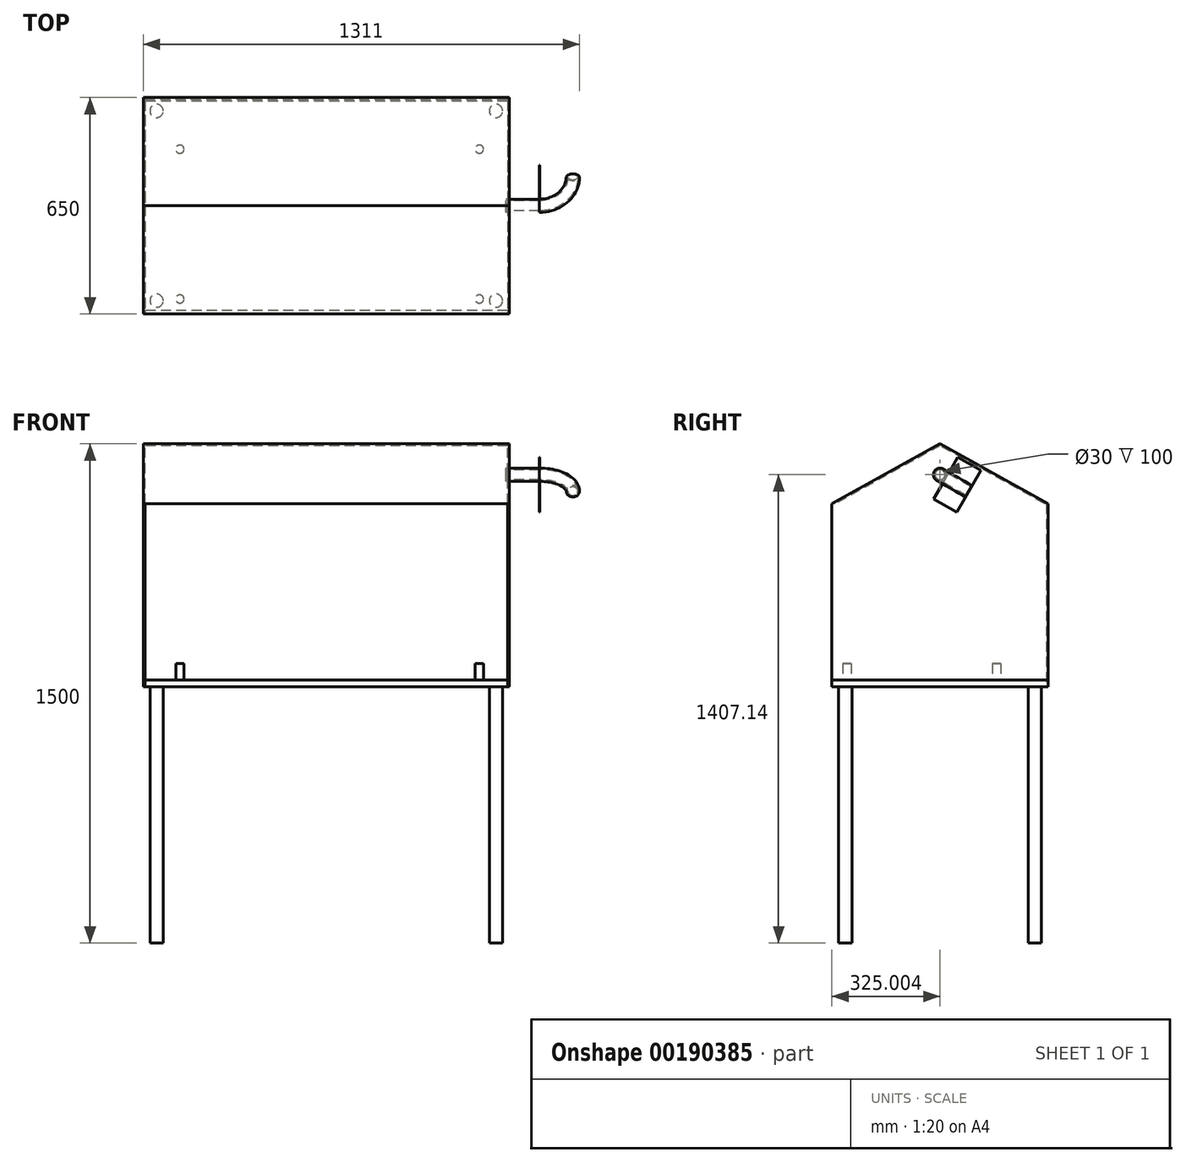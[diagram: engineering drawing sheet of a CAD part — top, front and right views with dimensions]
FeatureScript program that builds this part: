
annotation { "Feature Type Name" : "Feature", "Feature Type Description" : "" }
export const myFeature = defineFeature(function(context is Context, id is Id, definition is map)
    precondition{}
    {
        {
            var Q0;
            Q0=qCreatedBy(makeId("Top.planeOp"),FACE);
            var sketch = newSketch(context, id + "F0", { "sketchPlane" : qUnion([Q0])});
            skLineSegment(sketch, "E0.bottom", {"start": v(-6.1, 666.7) * mm, "end": v(1093.9, 666.7) * mm});
            skLineSegment(sketch, "E0.top", {"start": v(-6.1, 16.7) * mm, "end": v(1093.9, 16.7) * mm});
            skLineSegment(sketch, "E0.left", {"start": v(-6.1, 666.7) * mm, "end": v(-6.1, 16.7) * mm});
            skLineSegment(sketch, "E0.right", {"start": v(1093.9, 666.7) * mm, "end": v(1093.9, 16.7) * mm});
            skLineSegment(sketch, "E1.0", {"start": v(33.9, 626.7) * mm, "end": v(1053.9, 626.7) * mm, "construction": true});
            skLineSegment(sketch, "E1.1", {"start": v(33.9, 626.7) * mm, "end": v(33.9, 56.7) * mm, "construction": true});
            skLineSegment(sketch, "E1.2", {"start": v(33.9, 56.7) * mm, "end": v(1053.9, 56.7) * mm, "construction": true});
            skLineSegment(sketch, "E1.3", {"start": v(1053.9, 626.7) * mm, "end": v(1053.9, 56.7) * mm, "construction": true});
            skCircle(sketch, "E2", {"center": v(33.9, 626.7) * mm, "radius": 20 * mm});
            skCircle(sketch, "E3", {"center": v(1053.9, 626.7) * mm, "radius": 20 * mm});
            skCircle(sketch, "E4", {"center": v(33.9, 56.7) * mm, "radius": 20 * mm});
            skCircle(sketch, "E5", {"center": v(1053.9, 56.7) * mm, "radius": 20 * mm});
            skLineSegment(sketch, "E6.0", {"start": v(38.9, 621.7) * mm, "end": v(1048.9, 621.7) * mm, "construction": true});
            skLineSegment(sketch, "E6.1", {"start": v(38.9, 621.7) * mm, "end": v(38.9, 61.7) * mm, "construction": true});
            skLineSegment(sketch, "E6.2", {"start": v(38.9, 61.7) * mm, "end": v(1048.9, 61.7) * mm, "construction": true});
            skLineSegment(sketch, "E6.3", {"start": v(1048.9, 621.7) * mm, "end": v(1048.9, 61.7) * mm, "construction": true});
            skLineSegment(sketch, "E7", {"start": v(1098.9, 16.7) * mm, "end": v(1103.9, 16.7) * mm});
            skLineSegment(sketch, "E8", {"start": v(-11.1, 16.7) * mm, "end": v(-16.1, 16.7) * mm});
            skSolve(sketch);
        }
        {
            var Q0;
            Q0=makeQuery(id+"F0.imprint","IMPRINT",FACE,{"disambiguationData":[TD([[makeQuery(id+"F0.imprint","IMPRINT",EDGE,{"derivedFrom":sQuery(id+"F0.wireOp",EDGE,"E0.bottom")}),-1.0]])]});
            var Q1;
            Q1=makeQuery(id+"F0.imprint","IMPRINT",FACE,{"disambiguationData":[TD([[makeQuery(id+"F0.imprint","IMPRINT",EDGE,{"derivedFrom":sQuery(id+"F0.wireOp",EDGE,"E3")}),1.0]])]});
            var Q2;
            Q2=makeQuery(id+"F0.imprint","IMPRINT",FACE,{"disambiguationData":[TD([[makeQuery(id+"F0.imprint","IMPRINT",EDGE,{"derivedFrom":sQuery(id+"F0.wireOp",EDGE,"E5")}),1.0]])]});
            var Q3;
            Q3=makeQuery(id+"F0.imprint","IMPRINT",FACE,{"disambiguationData":[TD([[makeQuery(id+"F0.imprint","IMPRINT",EDGE,{"derivedFrom":sQuery(id+"F0.wireOp",EDGE,"E4")}),1.0]])]});
            var Q4;
            Q4=makeQuery(id+"F0.imprint","IMPRINT",FACE,{"disambiguationData":[TD([[makeQuery(id+"F0.imprint","IMPRINT",EDGE,{"derivedFrom":sQuery(id+"F0.wireOp",EDGE,"E2")}),1.0]])]});
            extrude(context, id + "F1", {"entities" : qUnion([Q0, Q1, Q2, Q3, Q4]), "depth" : 20 * mm});
        }
        {
            var Q0;
            Q0=makeQuery(id+"F0.imprint","IMPRINT",FACE,{"disambiguationData":[TD([[makeQuery(id+"F0.imprint","IMPRINT",EDGE,{"derivedFrom":sQuery(id+"F0.wireOp",EDGE,"E5")}),1.0]])]});
            var Q1;
            Q1=makeQuery(id+"F0.imprint","IMPRINT",FACE,{"disambiguationData":[TD([[makeQuery(id+"F0.imprint","IMPRINT",EDGE,{"derivedFrom":sQuery(id+"F0.wireOp",EDGE,"E3")}),1.0]])]});
            var Q2;
            Q2=makeQuery(id+"F0.imprint","IMPRINT",FACE,{"disambiguationData":[TD([[makeQuery(id+"F0.imprint","IMPRINT",EDGE,{"derivedFrom":sQuery(id+"F0.wireOp",EDGE,"E2")}),1.0]])]});
            var Q3;
            Q3=makeQuery(id+"F0.imprint","IMPRINT",FACE,{"disambiguationData":[TD([[makeQuery(id+"F0.imprint","IMPRINT",EDGE,{"derivedFrom":sQuery(id+"F0.wireOp",EDGE,"E4")}),1.0]])]});
            extrude(context, id + "F2", {"entities" : qUnion([Q0, Q1, Q2, Q3]), "operationType" : NewBodyOperationType.ADD, "oppositeDirection" : true, "depth" : 770 * mm});
        }
        {
            var Q0;
            Q0=makeQuery(id+"F1.opExtrude","CAP_FACE",FACE,{"disambiguationData":[OSD([sQuery(id+"F0.wireOp",EDGE,"E0.bottom"),sQuery(id+"F0.wireOp",EDGE,"E0.top"),sQuery(id+"F0.wireOp",EDGE,"E0.left"),sQuery(id+"F0.wireOp",EDGE,"E0.right")])],"isStart":false});
            var sketch = newSketch(context, id + "F3", { "sketchPlane" : qUnion([Q0])});
            skLineSegment(sketch, "E9.bottom", {"start": v(-6.1, 16.7) * mm, "end": v(1093.9, 16.7) * mm, "construction": true});
            skLineSegment(sketch, "E9.top", {"start": v(-6.1, 666.7) * mm, "end": v(1093.9, 666.7) * mm, "construction": true});
            skLineSegment(sketch, "E9.left", {"start": v(-6.1, 16.7) * mm, "end": v(-6.1, 666.7) * mm, "construction": true});
            skLineSegment(sketch, "E9.right", {"start": v(1093.9, 16.7) * mm, "end": v(1093.9, 666.7) * mm, "construction": true});
            skLineSegment(sketch, "E10.0", {"start": v(33.9, 626.7) * mm, "end": v(1003.9, 626.7) * mm, "construction": true});
            skLineSegment(sketch, "E10.1", {"start": v(33.9, 56.7) * mm, "end": v(33.9, 626.7) * mm, "construction": true});
            skLineSegment(sketch, "E10.2", {"start": v(33.9, 56.7) * mm, "end": v(1003.9, 56.7) * mm, "construction": true});
            skLineSegment(sketch, "E10.3", {"start": v(1003.9, 56.7) * mm, "end": v(1003.9, 626.7) * mm, "construction": true});
            skLineSegment(sketch, "E11", {"start": v(33.9, 511.7) * mm, "end": v(1003.9, 511.7) * mm, "construction": true});
            skLineSegment(sketch, "E12", {"start": v(33.9, 61.7) * mm, "end": v(1003.9, 61.7) * mm, "construction": true});
            skLineSegment(sketch, "E13.bottom", {"start": v(1003.9, 511.7) * mm, "end": v(103.9, 511.7) * mm, "construction": true});
            skLineSegment(sketch, "E13.top", {"start": v(1003.9, 61.7) * mm, "end": v(103.9, 61.7) * mm, "construction": true});
            skLineSegment(sketch, "E13.left", {"start": v(1003.9, 511.7) * mm, "end": v(1003.9, 61.7) * mm, "construction": true});
            skLineSegment(sketch, "E13.right", {"start": v(103.9, 511.7) * mm, "end": v(103.9, 61.7) * mm, "construction": true});
            skCircle(sketch, "E14", {"center": v(103.9, 511.7) * mm, "radius": 12.5 * mm});
            skCircle(sketch, "E15", {"center": v(103.9, 61.7) * mm, "radius": 12.5 * mm});
            skCircle(sketch, "E16", {"center": v(1003.9, 511.7) * mm, "radius": 12.5 * mm});
            skCircle(sketch, "E17", {"center": v(1003.9, 61.7) * mm, "radius": 12.5 * mm});
            skSolve(sketch);
        }
        {
            var Q0;
            Q0=makeQuery(id+"F3.imprint","IMPRINT",FACE,{"disambiguationData":[TD([[makeQuery(id+"F3.imprint","IMPRINT",EDGE,{"derivedFrom":sQuery(id+"F3.wireOp",EDGE,"E16")}),1.0]])]});
            var Q1;
            Q1=makeQuery(id+"F3.imprint","IMPRINT",FACE,{"disambiguationData":[TD([[makeQuery(id+"F3.imprint","IMPRINT",EDGE,{"derivedFrom":sQuery(id+"F3.wireOp",EDGE,"E17")}),1.0]])]});
            var Q2;
            Q2=makeQuery(id+"F3.imprint","IMPRINT",FACE,{"disambiguationData":[TD([[makeQuery(id+"F3.imprint","IMPRINT",EDGE,{"derivedFrom":sQuery(id+"F3.wireOp",EDGE,"E15")}),1.0]])]});
            var Q3;
            Q3=makeQuery(id+"F3.imprint","IMPRINT",FACE,{"disambiguationData":[TD([[makeQuery(id+"F3.imprint","IMPRINT",EDGE,{"derivedFrom":sQuery(id+"F3.wireOp",EDGE,"E14")}),1.0]])]});
            extrude(context, id + "F4", {"entities" : qUnion([Q0, Q1, Q2, Q3]), "operationType" : NewBodyOperationType.ADD, "depth" : 50 * mm});
        }
        {
            var Q0;
            Q0=qCreatedBy(makeId("Top.planeOp"),FACE);
            var sketch = newSketch(context, id + "F5", { "sketchPlane" : qUnion([Q0])});
            skLineSegment(sketch, "E18.0", {"start": v(-1.1, 661.7) * mm, "end": v(-1.1, 16.7) * mm});
            skLineSegment(sketch, "E18.1", {"start": v(-1.1, 661.7) * mm, "end": v(1088.9, 661.7) * mm});
            skLineSegment(sketch, "E18.2", {"start": v(1088.9, 661.7) * mm, "end": v(1088.9, 16.7) * mm});
            skLineSegment(sketch, "E19.0", {"start": v(-6.1, 666.7) * mm, "end": v(-6.1, 16.7) * mm});
            skLineSegment(sketch, "E19.1", {"start": v(-6.1, 666.7) * mm, "end": v(1093.9, 666.7) * mm});
            skLineSegment(sketch, "E19.2", {"start": v(1093.9, 666.7) * mm, "end": v(1093.9, 16.7) * mm});
            skLineSegment(sketch, "E20", {"start": v(-6.1, 16.7) * mm, "end": v(-1.1, 16.7) * mm});
            skLineSegment(sketch, "E21", {"start": v(1088.9, 16.7) * mm, "end": v(1093.9, 16.7) * mm});
            skSolve(sketch);
        }
        {
            var Q0;
            Q0=makeQuery(id+"F5.imprint","IMPRINT",FACE,{"disambiguationData":[TD([[makeQuery(id+"F5.imprint","IMPRINT",EDGE,{"derivedFrom":sQuery(id+"F5.wireOp",EDGE,"E18.0")}),-1.0]])]});
            extrude(context, id + "F6", {"entities" : qUnion([Q0]), "depth" : 550 * mm});
        }
        {
            var Q0;
            Q0=makeQuery(id+"F6.opExtrude","SWEPT_FACE",FACE,{"disambiguationData":[OSD([sQuery(id+"F5.wireOp",EDGE,"E19.0")])]});
            var sketch = newSketch(context, id + "F7", { "sketchPlane" : qUnion([Q0])});
            skLineSegment(sketch, "E22", {"start": v(-666.7, 550) * mm, "end": v(-341.7, 730) * mm});
            skPoint(sketch, "E22.endSnap0", {"position": v(-341.7, 550) * mm});
            skLineSegment(sketch, "E23", {"start": v(-341.7, 730) * mm, "end": v(-16.7, 550) * mm});
            skLineSegment(sketch, "E24.0", {"start": v(-341.7, 724.28) * mm, "end": v(-27.02, 550) * mm});
            skLineSegment(sketch, "E24.1", {"start": v(-656.38, 550) * mm, "end": v(-341.7, 724.28) * mm});
            skLineSegment(sketch, "E25", {"start": v(-16.7, 550) * mm, "end": v(-666.7, 550) * mm});
            skCircle(sketch, "E26", {"center": v(-341.7, 637.14) * mm, "radius": 15 * mm});
            skPoint(sketch, "E26.centerSnap0", {"position": v(-499.04, 637.14) * mm});
            skCircle(sketch, "E27", {"center": v(-341.7, 637.14) * mm, "radius": 20 * mm});
            skSolve(sketch);
        }
        {
            var Q0;
            {var subQ3=sQuery(id+"F7.wireOp",EDGE,"E22");Q0=makeQuery(id+"F7.imprint","IMPRINT",FACE,{"disambiguationData":[TD([[makeQuery(id+"F7.imprint","IMPRINT",EDGE,{"derivedFrom":subQ3}),-1.0]])]});}
            extrude(context, id + "F8", {"entities" : qUnion([Q0]), "operationType" : NewBodyOperationType.ADD, "oppositeDirection" : true, "depth" : 1100 * mm});
        }
        {
            var Q0;
            {var subQ0=sQuery(id+"F7.wireOp",EDGE,"E24.0");Q0=makeQuery(id+"F7.imprint","IMPRINT",FACE,{"disambiguationData":[TD([[makeQuery(id+"F7.imprint","IMPRINT",EDGE,{"derivedFrom":subQ0}),-1.0]])]});}
            extrude(context, id + "F9", {"entities" : qUnion([Q0]), "operationType" : NewBodyOperationType.ADD, "oppositeDirection" : true, "depth" : 1100 * mm, "hasSecondDirection" : true, "secondDirectionOppositeDirection" : true, "secondDirectionDepth" : 1095 * mm});
        }
        {
            var Q0;
            {var subQ0=sQuery(id+"F7.wireOp",EDGE,"E24.0");Q0=makeQuery(id+"F7.imprint","IMPRINT",FACE,{"disambiguationData":[TD([[makeQuery(id+"F7.imprint","IMPRINT",EDGE,{"derivedFrom":subQ0}),-1.0]])]});}
            var Q1;
            Q1=makeQuery(id+"F7.imprint","IMPRINT",FACE,{"disambiguationData":[TD([[makeQuery(id+"F7.imprint","IMPRINT",EDGE,{"derivedFrom":sQuery(id+"F7.wireOp",EDGE,"E26")}),1.0]])]});
            var Q2;
            Q2=makeQuery(id+"F7.imprint","IMPRINT",FACE,{"disambiguationData":[TD([[makeQuery(id+"F7.imprint","IMPRINT",EDGE,{"derivedFrom":sQuery(id+"F7.wireOp",EDGE,"E26")}),-1.0]])]});
            extrude(context, id + "F10", {"entities" : qUnion([Q0, Q1, Q2]), "operationType" : NewBodyOperationType.ADD, "oppositeDirection" : true, "depth" : 5 * mm});
        }
        {
            var Q0;
            Q0=makeQuery(id+"F7.imprint","IMPRINT",FACE,{"disambiguationData":[TD([[makeQuery(id+"F7.imprint","IMPRINT",EDGE,{"derivedFrom":sQuery(id+"F7.wireOp",EDGE,"E26")}),-1.0]])]});
            extrude(context, id + "F11", {"entities" : qUnion([Q0]), "operationType" : NewBodyOperationType.ADD, "oppositeDirection" : true, "depth" : 1190 * mm, "hasSecondDirection" : true, "secondDirectionOppositeDirection" : true, "secondDirectionDepth" : 1090 * mm});
        }
        {
            var Q0;
            Q0=makeQuery(id+"F11.opExtrude","CAP_FACE",FACE,{"disambiguationData":[OSD([sQuery(id+"F7.wireOp",EDGE,"E26"),sQuery(id+"F7.wireOp",EDGE,"E27")])],"isStart":false});
            var sketch = newSketch(context, id + "F12", { "sketchPlane" : qUnion([Q0])});
            skLineSegment(sketch, "E28", {"start": v(359.04, 627.18) * mm, "end": v(322.86, 564.35) * mm});
            skLineSegment(sketch, "E29.bottom", {"start": v(322.86, 564.35) * mm, "end": v(395.23, 690) * mm});
            skLineSegment(sketch, "E29.top", {"start": v(392.18, 524.42) * mm, "end": v(464.55, 650.07) * mm});
            skLineSegment(sketch, "E29.left", {"start": v(322.86, 564.35) * mm, "end": v(392.18, 524.42) * mm});
            skLineSegment(sketch, "E29.right", {"start": v(395.23, 690) * mm, "end": v(464.55, 650.07) * mm});
            skPoint(sketch, "E30", {"position": v(359.04, 627.18) * mm});
            skSolve(sketch);
        }
        {
            var Q0;
            Q0=makeQuery(id+"F12.imprint","IMPRINT",FACE,{"disambiguationData":[TD([[makeQuery(id+"F12.imprint","IMPRINT",EDGE,{"derivedFrom":sQuery(id+"F12.wireOp",EDGE,"E29.top")}),1.0]])]});
            extrude(context, id + "F13", {"entities" : qUnion([Q0]), "depth" : 1 * mm});
        }
        {
            var Q0;
            Q0=makeQuery(id+"F11.opExtrude","CAP_FACE",FACE,{"disambiguationData":[OSD([sQuery(id+"F7.wireOp",EDGE,"E26"),sQuery(id+"F7.wireOp",EDGE,"E27")])],"isStart":false});
            var Q1;
            Q1=makeQuery(id+"F13.opExtrude","CAP_EDGE",EDGE,{"disambiguationData":[OSD([sQuery(id+"F12.wireOp",EDGE,"E29.top")])],"isStart":false});
            revolve(context, id + "F14", {"operationType" : NewBodyOperationType.ADD, "entities" : qUnion([Q0]), "axis" : qUnion([Q1]), "revolveType" : RevolveType.ONE_DIRECTION, "angle" : 90 * degree});
        }
    });
